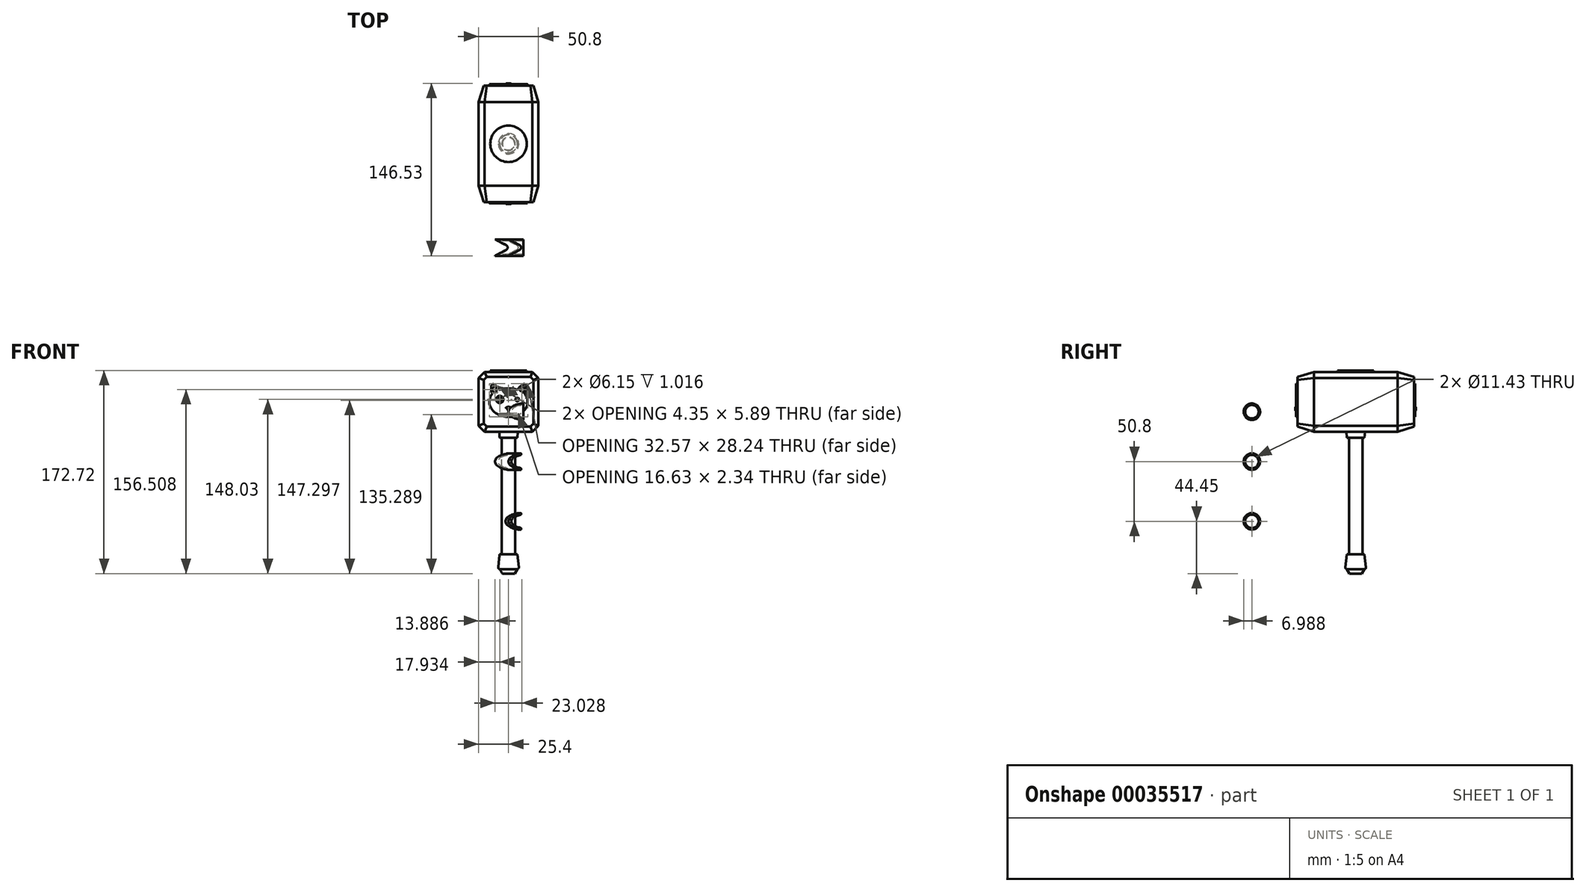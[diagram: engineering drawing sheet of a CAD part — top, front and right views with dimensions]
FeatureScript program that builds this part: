
annotation { "Feature Type Name" : "Feature", "Feature Type Description" : "" }
export const myFeature = defineFeature(function(context is Context, id is Id, definition is map)
    precondition{}
    {
        {
            var Q0;
            Q0=qCreatedBy(makeId("Front.planeOp"),FACE);
            var sketch = newSketch(context, id + "F0", { "sketchPlane" : qUnion([Q0])});
            skLineSegment(sketch, "E0.rect.bottom", {"start": v(25.4, 25.4) * mm, "end": v(-25.4, 25.4) * mm});
            skLineSegment(sketch, "E0.rect.top", {"start": v(25.4, -25.4) * mm, "end": v(-25.4, -25.4) * mm});
            skLineSegment(sketch, "E0.rect.left", {"start": v(25.4, 25.4) * mm, "end": v(25.4, -25.4) * mm});
            skLineSegment(sketch, "E0.rect.right", {"start": v(-25.4, 25.4) * mm, "end": v(-25.4, -25.4) * mm});
            skPoint(sketch, "E0.rect.middle", {"position": v(0, 0) * mm});
            skSolve(sketch);
        }
        {
            var Q0;
            Q0=makeQuery(id+"F0.imprint","IMPRINT",FACE,{"disambiguationData":[TD([[makeQuery(id+"F0.imprint","IMPRINT",EDGE,{"derivedFrom":sQuery(id+"F0.wireOp",EDGE,"E0.rect.bottom")}),1.0]])]});
            extrude(context, id + "F1", {"entities" : qUnion([Q0]), "endBound" : BoundingType.SYMMETRIC, "depth" : 71.12 * mm});
        }
        {
            var Q0;
            Q0=makeQuery(id+"F1.opExtrude","SWEPT_EDGE",EDGE,{"disambiguationData":[OSD([sQuery(id+"F0.wireOp",EDGE,"E0.rect.bottom"),sQuery(id+"F0.wireOp",EDGE,"E0.rect.left")])]});
            var Q1;
            Q1=makeQuery(id+"F1.opExtrude","SWEPT_EDGE",EDGE,{"disambiguationData":[OSD([sQuery(id+"F0.wireOp",EDGE,"E0.rect.top"),sQuery(id+"F0.wireOp",EDGE,"E0.rect.left")])]});
            var Q2;
            Q2=makeQuery(id+"F1.opExtrude","SWEPT_EDGE",EDGE,{"disambiguationData":[OSD([sQuery(id+"F0.wireOp",EDGE,"E0.rect.top"),sQuery(id+"F0.wireOp",EDGE,"E0.rect.right")])]});
            var Q3;
            Q3=makeQuery(id+"F1.opExtrude","SWEPT_EDGE",EDGE,{"disambiguationData":[OSD([sQuery(id+"F0.wireOp",EDGE,"E0.rect.bottom"),sQuery(id+"F0.wireOp",EDGE,"E0.rect.right")])]});
            chamfer(context, id + "F2", {"entities" : qUnion([Q0, Q1, Q2, Q3]), "width" : 5.08 * mm, "tangentPropagation" : true});
        }
        {
            var Q0;
            Q0=makeQuery(id+"F1.opExtrude","CAP_FACE",FACE,{"disambiguationData":[OSD([sQuery(id+"F0.wireOp",EDGE,"E0.rect.bottom"),sQuery(id+"F0.wireOp",EDGE,"E0.rect.top"),sQuery(id+"F0.wireOp",EDGE,"E0.rect.left"),sQuery(id+"F0.wireOp",EDGE,"E0.rect.right")])],"isStart":false});
            var sketch = newSketch(context, id + "F3", { "sketchPlane" : qUnion([Q0])});
            skLineSegment(sketch, "E1.0.0", {"start": v(20.32, 25.4) * mm, "end": v(-20.32, 25.4) * mm});
            skLineSegment(sketch, "E1.0.1", {"start": v(-20.32, 25.4) * mm, "end": v(-25.4, 20.32) * mm});
            skLineSegment(sketch, "E1.0.2", {"start": v(-25.4, 20.32) * mm, "end": v(-25.4, -20.32) * mm});
            skLineSegment(sketch, "E1.0.3", {"start": v(-25.4, -20.32) * mm, "end": v(-20.32, -25.4) * mm});
            skLineSegment(sketch, "E1.0.4", {"start": v(-20.32, -25.4) * mm, "end": v(20.32, -25.4) * mm});
            skLineSegment(sketch, "E1.0.5", {"start": v(20.32, -25.4) * mm, "end": v(25.4, -20.32) * mm});
            skLineSegment(sketch, "E1.0.6", {"start": v(25.4, -20.32) * mm, "end": v(25.4, 20.32) * mm});
            skLineSegment(sketch, "E1.0.7", {"start": v(25.4, 20.32) * mm, "end": v(20.32, 25.4) * mm});
            skSolve(sketch);
        }
        {
            var Q0;
            Q0=makeQuery(id+"F1.opExtrude","CAP_FACE",FACE,{"disambiguationData":[OSD([sQuery(id+"F0.wireOp",EDGE,"E0.rect.bottom"),sQuery(id+"F0.wireOp",EDGE,"E0.rect.top"),sQuery(id+"F0.wireOp",EDGE,"E0.rect.left"),sQuery(id+"F0.wireOp",EDGE,"E0.rect.right")])],"isStart":false});
            var Q1;
            Q1=makeQuery(id+"F3.imprint","IMPRINT",FACE,{"disambiguationData":[TD([[makeQuery(id+"F3.imprint","IMPRINT",EDGE,{"derivedFrom":sQuery(id+"F3.wireOp",EDGE,"E1.0.0")}),1.0]])]});
            extrude(context, id + "F4", {"entities" : qUnion([Q0, Q1]), "operationType" : NewBodyOperationType.ADD, "depth" : 13.97 * mm, "hasDraft" : true, "draftAngle" : 17 * degree, "draftPullDirection" : true});
        }
        {
            var Q0;
            Q0=makeQuery(id+"F1.opExtrude","CAP_FACE",FACE,{"disambiguationData":[OSD([sQuery(id+"F0.wireOp",EDGE,"E0.rect.bottom"),sQuery(id+"F0.wireOp",EDGE,"E0.rect.top"),sQuery(id+"F0.wireOp",EDGE,"E0.rect.left"),sQuery(id+"F0.wireOp",EDGE,"E0.rect.right")])],"isStart":true});
            var sketch = newSketch(context, id + "F5", { "sketchPlane" : qUnion([Q0])});
            skLineSegment(sketch, "E2.0.0", {"start": v(25.4, -20.32) * mm, "end": v(25.4, 20.32) * mm});
            skLineSegment(sketch, "E2.0.1", {"start": v(25.4, 20.32) * mm, "end": v(20.32, 25.4) * mm});
            skLineSegment(sketch, "E2.0.2", {"start": v(20.32, 25.4) * mm, "end": v(-20.32, 25.4) * mm});
            skLineSegment(sketch, "E2.0.3", {"start": v(-20.32, 25.4) * mm, "end": v(-25.4, 20.32) * mm});
            skLineSegment(sketch, "E2.0.4", {"start": v(-25.4, 20.32) * mm, "end": v(-25.4, -20.32) * mm});
            skLineSegment(sketch, "E2.0.5", {"start": v(-25.4, -20.32) * mm, "end": v(-20.32, -25.4) * mm});
            skLineSegment(sketch, "E2.0.6", {"start": v(-20.32, -25.4) * mm, "end": v(20.32, -25.4) * mm});
            skLineSegment(sketch, "E2.0.7", {"start": v(20.32, -25.4) * mm, "end": v(25.4, -20.32) * mm});
            skSolve(sketch);
        }
        {
            var Q0;
            Q0=makeQuery(id+"F5.imprint","IMPRINT",FACE,{"disambiguationData":[TD([[makeQuery(id+"F5.imprint","IMPRINT",EDGE,{"derivedFrom":sQuery(id+"F5.wireOp",EDGE,"E2.0.0")}),-1.0]])]});
            extrude(context, id + "F6", {"entities" : qUnion([Q0]), "operationType" : NewBodyOperationType.ADD, "depth" : 13.97 * mm, "hasDraft" : true, "draftAngle" : 17 * degree, "draftPullDirection" : true});
        }
        {
            var Q0;
            Q0=makeQuery(id+"F1.opExtrude","SWEPT_FACE",FACE,{"disambiguationData":[OSD([sQuery(id+"F0.wireOp",EDGE,"E0.rect.bottom")])]});
            var sketch = newSketch(context, id + "F7", { "sketchPlane" : qUnion([Q0])});
            skCircle(sketch, "E3", {"center": v(0, 0) * mm, "radius": 15.5 * mm});
            skSolve(sketch);
        }
        {
            var Q0;
            Q0=qSketchRegion(id+"F7",true);
            extrude(context, id + "F8", {"entities" : qUnion([Q0]), "operationType" : NewBodyOperationType.ADD, "depth" : 1.27 * mm});
        }
        {
            var Q0;
            Q0=makeQuery(id+"F1.opExtrude","SWEPT_FACE",FACE,{"disambiguationData":[OSD([sQuery(id+"F0.wireOp",EDGE,"E0.rect.top")])]});
            var sketch = newSketch(context, id + "F9", { "sketchPlane" : qUnion([Q0])});
            skCircle(sketch, "E4", {"center": v(0, 0) * mm, "radius": 7.93 * mm});
            skSolve(sketch);
        }
        {
            var Q0;
            Q0=qSketchRegion(id+"F9",true);
            extrude(context, id + "F10", {"entities" : qUnion([Q0]), "operationType" : NewBodyOperationType.ADD, "depth" : 5.08 * mm, "hasDraft" : true, "draftAngle" : 5 * degree, "draftPullDirection" : true});
        }
        {
            var Q0;
            Q0=makeQuery(id+"F10.opExtrude","CAP_FACE",FACE,{"disambiguationData":[OSD([sQuery(id+"F9.wireOp",EDGE,"E4")])],"isStart":false});
            var sketch = newSketch(context, id + "F11", { "sketchPlane" : qUnion([Q0])});
            skCircle(sketch, "E5", {"center": v(0, 0) * mm, "radius": 6.99 * mm});
            skCircle(sketch, "E6", {"center": v(0, 0) * mm, "radius": 5.72 * mm});
            skSolve(sketch);
        }
        {
            var Q0;
            Q0=makeQuery(id+"F11.imprint","IMPRINT",FACE,{"disambiguationData":[TD([[makeQuery(id+"F11.imprint","IMPRINT",EDGE,{"derivedFrom":sQuery(id+"F11.wireOp",EDGE,"E6")}),1.0]])]});
            extrude(context, id + "F12", {"entities" : qUnion([Q0]), "operationType" : NewBodyOperationType.ADD, "depth" : 99.06 * mm});
        }
        {
            var Q0;
            Q0=makeQuery(id+"F12.opExtrude","CAP_FACE",FACE,{"disambiguationData":[OSD([sQuery(id+"F11.wireOp",EDGE,"E6")])],"isStart":false});
            var sketch = newSketch(context, id + "F13", { "sketchPlane" : qUnion([Q0])});
            skCircle(sketch, "E7", {"center": v(0, 0) * mm, "radius": 7.55 * mm});
            skSolve(sketch);
        }
        {
            var Q0;
            Q0=qSketchRegion(id+"F13",true);
            extrude(context, id + "F14", {"entities" : qUnion([Q0]), "depth" : 12.7 * mm, "hasDraft" : true, "draftAngle" : 6 * degree});
        }
        {
            var Q0;
            Q0=makeQuery(id+"F14.opExtrude","CAP_EDGE",EDGE,{"disambiguationData":[OSD([sQuery(id+"F13.wireOp",EDGE,"E7")])],"isStart":false});
            fillet(context, id + "F15", {"entities" : qUnion([Q0]), "radius" : 1.27 * mm, "tangentPropagation" : true, "allowEdgeOverflow" : false});
        }
        {
            var Q0;
            Q0=makeQuery(id+"F14.opExtrude","CAP_FACE",FACE,{"disambiguationData":[OSD([sQuery(id+"F13.wireOp",EDGE,"E7")])],"isStart":false});
            var sketch = newSketch(context, id + "F16", { "sketchPlane" : qUnion([Q0])});
            skCircle(sketch, "E8.0", {"center": v(0, 0) * mm, "radius": 7.47 * mm});
            skSolve(sketch);
        }
        {
            var Q0;
            Q0=qSketchRegion(id+"F16",true);
            extrude(context, id + "F17", {"entities" : qUnion([Q0]), "operationType" : NewBodyOperationType.ADD, "depth" : 3.8 * mm, "hasDraft" : true, "draftAngle" : 30 * degree, "draftPullDirection" : true});
        }
        {
            var Q0;
            Q0=qCreatedBy(makeId("Right.planeOp"),FACE);
            var sketch = newSketch(context, id + "F18", { "sketchPlane" : qUnion([Q0])});
            skCircle(sketch, "E9", {"center": v(-88.23, -8.44) * mm, "radius": 6.99 * mm});
            skCircle(sketch, "E10", {"center": v(-88.23, -8.44) * mm, "radius": 5.72 * mm});
            skSolve(sketch);
        }
        {
            var Q0;
            Q0=qSketchRegion(id+"F18",true);
            extrude(context, id + "F19", {"entities" : qUnion([Q0]), "depth" : 12.7 * mm});
        }
        {
            var Q0;
            Q0=qCreatedBy(makeId("Top.planeOp"),FACE);
            var sketch = newSketch(context, id + "F20", { "sketchPlane" : qUnion([Q0])});
            skLineSegment(sketch, "E11.0", {"start": v(12.7, -81.25) * mm, "end": v(12.7, -95.22) * mm});
            skLineSegment(sketch, "E12.0", {"start": v(0, -81.25) * mm, "end": v(0, -88.23) * mm});
            skLineSegment(sketch, "E13", {"start": v(0, -81.25) * mm, "end": v(9.4, -86.15) * mm});
            skLineSegment(sketch, "E14.MirrorCS", {"start": v(0, -95.22) * mm, "end": v(9.4, -90.31) * mm});
            skArc(sketch, "E15", {"start": v(9.4, -90.31) * mm, "mid": v(10.65, -88.23) * mm, "end": v(9.4, -86.15) * mm});
            skPoint(sketch, "E16.orphan", {"position": v(0, -95.22) * mm});
            skLineSegment(sketch, "E17", {"start": v(0, -88.23) * mm, "end": v(0, -95.22) * mm});
            skLineSegment(sketch, "E18", {"start": v(0, -95.22) * mm, "end": v(-11.43, -95.22) * mm});
            skLineSegment(sketch, "E19", {"start": v(0, -81.25) * mm, "end": v(-11.43, -81.25) * mm});
            skLineSegment(sketch, "E20", {"start": v(-11.43, -95.22) * mm, "end": v(-2.04, -90.31) * mm});
            skLineSegment(sketch, "E21", {"start": v(0, -88.23) * mm, "end": v(8.3, -88.23) * mm});
            skLineSegment(sketch, "E22.MirrorCS", {"start": v(-11.43, -81.25) * mm, "end": v(-2.04, -86.15) * mm});
            skArc(sketch, "E23", {"start": v(-2.04, -90.31) * mm, "mid": v(-0.78, -88.23) * mm, "end": v(-2.04, -86.15) * mm});
            skSolve(sketch);
        }
        {
            var Q0;
            Q0=qSketchRegion(id+"F20",true);
            extrude(context, id + "F21", {"entities" : qUnion([Q0]), "operationType" : NewBodyOperationType.REMOVE, "oppositeDirection" : true, "depth" : 25.4 * mm});
        }
        {
            var Q0;
            Q0=qCreatedBy(makeId("Right.planeOp"),FACE);
            var sketch = newSketch(context, id + "F22", { "sketchPlane" : qUnion([Q0])});
            skCircle(sketch, "E24.0", {"center": v(-88.23, -8.44) * mm, "radius": 5.72 * mm});
            skLineSegment(sketch, "E25", {"start": v(-88.23, -8.44) * mm, "end": v(-88.23, 15.5) * mm});
            skCircle(sketch, "E26", {"center": v(-88.23, 15.5) * mm, "radius": 6.99 * mm});
            skCircle(sketch, "E27", {"center": v(-88.23, 15.5) * mm, "radius": 5.72 * mm});
            skSolve(sketch);
        }
        {
            var Q0;
            Q0=makeQuery(id+"F22.imprint","IMPRINT",FACE,{"disambiguationData":[TD([[makeQuery(id+"F22.imprint","IMPRINT",EDGE,{"derivedFrom":sQuery(id+"F22.wireOp",EDGE,"E26")}),1.0]])]});
            extrude(context, id + "F23", {"entities" : qUnion([Q0]), "endBound" : BoundingType.SYMMETRIC, "depth" : 22.86 * mm});
        }
        {
            var Q0;
            Q0=qSketchRegion(id+"F20",true);
            extrude(context, id + "F24", {"entities" : qUnion([Q0]), "operationType" : NewBodyOperationType.REMOVE, "endBound" : BoundingType.SYMMETRIC, "oppositeDirection" : true, "depth" : 508 * mm});
        }
        {
            var Q0;
            Q0=makeQuery(id+"F24.boolean.opBoolean","SPLIT",BODY,{"disambiguationData":[OD(0.0)],"derivedFrom":makeQuery(id+"F23.opExtrude","SWEPT_BODY",BODY,{"disambiguationData":[OSD([sQuery(id+"F22.wireOp",EDGE,"E26"),sQuery(id+"F22.wireOp",EDGE,"E27")])]})});
            deleteBodies(context, id + "F25", {"entities" : qUnion([Q0])});
        }
        {
            var Q0;
            Q0=qCreatedBy(makeId("Right.planeOp"),FACE);
            var sketch = newSketch(context, id + "F26", { "sketchPlane" : qUnion([Q0])});
            skCircle(sketch, "E28.0", {"center": v(-88.23, -8.44) * mm, "radius": 5.72 * mm});
            skLineSegment(sketch, "E29", {"start": v(-88.23, -8.44) * mm, "end": v(-88.23, -50.8) * mm});
            skLineSegment(sketch, "E30", {"start": v(0, 0) * mm, "end": v(-109.96, 0) * mm});
            skCircle(sketch, "E31", {"center": v(-88.23, -50.8) * mm, "radius": 6.99 * mm});
            skCircle(sketch, "E32", {"center": v(-88.23, -50.8) * mm, "radius": 5.72 * mm});
            skSolve(sketch);
        }
        {
            var Q0;
            Q0=makeQuery(id+"F26.imprint","IMPRINT",FACE,{"disambiguationData":[TD([[makeQuery(id+"F26.imprint","IMPRINT",EDGE,{"derivedFrom":sQuery(id+"F26.wireOp",EDGE,"E31")}),1.0]])]});
            extrude(context, id + "F27", {"entities" : qUnion([Q0]), "endBound" : BoundingType.SYMMETRIC, "depth" : 25.4 * mm});
        }
        {
            var Q0;
            Q0=qCreatedBy(makeId("Top.planeOp"),FACE);
            cPlane(context, id + "F28", {"entities" : qUnion([Q0]), "cplaneType" : CPlaneType.OFFSET, "offset" : 50.8 * mm, "oppositeDirection" : true, "width" : 152.4 * mm, "height" : 152.4 * mm});
        }
        {
            var Q0;
            Q0=qCreatedBy(id+"F28.planeOp",FACE);
            var sketch = newSketch(context, id + "F29", { "sketchPlane" : qUnion([Q0])});
            skLineSegment(sketch, "E33.0", {"start": v(9.4, -86.15) * mm, "end": v(0, -81.25) * mm});
            skArc(sketch, "E34.0", {"start": v(9.4, -86.15) * mm, "mid": v(10.65, -88.23) * mm, "end": v(9.4, -90.31) * mm});
            skLineSegment(sketch, "E35.0", {"start": v(9.4, -90.31) * mm, "end": v(0, -95.22) * mm});
            skLineSegment(sketch, "E36", {"start": v(12.7, -95.22) * mm, "end": v(0, -95.22) * mm});
            skLineSegment(sketch, "E37.0", {"start": v(12.7, -81.25) * mm, "end": v(12.7, -95.22) * mm});
            skLineSegment(sketch, "E38", {"start": v(0, -81.25) * mm, "end": v(12.7, -81.25) * mm});
            skLineSegment(sketch, "E39.0", {"start": v(-12.7, -81.25) * mm, "end": v(-12.7, -95.22) * mm});
            skArc(sketch, "E40.0", {"start": v(-2.04, -86.15) * mm, "mid": v(-0.78, -88.23) * mm, "end": v(-2.04, -90.31) * mm});
            skLineSegment(sketch, "E41.0", {"start": v(-2.04, -86.15) * mm, "end": v(-11.43, -81.25) * mm});
            skLineSegment(sketch, "E42.0", {"start": v(-2.04, -90.31) * mm, "end": v(-11.43, -95.22) * mm});
            skLineSegment(sketch, "E43", {"start": v(-11.43, -81.25) * mm, "end": v(-12.7, -81.25) * mm});
            skLineSegment(sketch, "E44", {"start": v(-11.43, -95.22) * mm, "end": v(-12.7, -95.22) * mm});
            skSolve(sketch);
        }
        {
            var Q0;
            Q0=qSketchRegion(id+"F29",true);
            extrude(context, id + "F30", {"entities" : qUnion([Q0]), "operationType" : NewBodyOperationType.REMOVE, "endBound" : BoundingType.SYMMETRIC, "oppositeDirection" : true, "depth" : 25.4 * mm});
        }
        {
            var Q0;
            Q0=qCreatedBy(makeId("Right.planeOp"),FACE);
            var sketch = newSketch(context, id + "F31", { "sketchPlane" : qUnion([Q0])});
            skArc(sketch, "E45.0", {"start": v(-86.15, -56.12) * mm, "mid": v(-82.52, -50.8) * mm, "end": v(-86.15, -45.48) * mm});
            skLineSegment(sketch, "E46", {"start": v(-88.23, -50.8) * mm, "end": v(-88.23, -101.6) * mm});
            skCircle(sketch, "E47", {"center": v(-88.23, -101.6) * mm, "radius": 6.99 * mm});
            skCircle(sketch, "E48", {"center": v(-88.23, -101.6) * mm, "radius": 5.72 * mm});
            skSolve(sketch);
        }
        {
            var Q0;
            Q0=makeQuery(id+"F31.imprint","IMPRINT",FACE,{"disambiguationData":[TD([[makeQuery(id+"F31.imprint","IMPRINT",EDGE,{"derivedFrom":sQuery(id+"F31.wireOp",EDGE,"E47")}),1.0]])]});
            extrude(context, id + "F32", {"entities" : qUnion([Q0]), "endBound" : BoundingType.SYMMETRIC, "depth" : 25.4 * mm});
        }
        {
            var Q0;
            Q0=qCreatedBy(id+"F28.planeOp",FACE);
            cPlane(context, id + "F33", {"entities" : qUnion([Q0]), "cplaneType" : CPlaneType.OFFSET, "offset" : 50.8 * mm, "oppositeDirection" : true, "width" : 152.4 * mm, "height" : 152.4 * mm});
        }
        {
            var Q0;
            Q0=qCreatedBy(id+"F33.planeOp",FACE);
            var sketch = newSketch(context, id + "F34", { "sketchPlane" : qUnion([Q0])});
            skLineSegment(sketch, "E49.0", {"start": v(9.4, -86.15) * mm, "end": v(0, -81.25) * mm});
            skArc(sketch, "E50.0", {"start": v(9.4, -86.15) * mm, "mid": v(10.65, -88.23) * mm, "end": v(9.4, -90.31) * mm});
            skLineSegment(sketch, "E51.0", {"start": v(9.4, -90.31) * mm, "end": v(0, -95.22) * mm});
            skLineSegment(sketch, "E52", {"start": v(-2.54, -95.22) * mm, "end": v(-2.54, -81.25) * mm});
            skLineSegment(sketch, "E53", {"start": v(-2.54, -95.22) * mm, "end": v(6.85, -90.31) * mm});
            skLineSegment(sketch, "E54.MirrorCS", {"start": v(-2.54, -81.25) * mm, "end": v(6.85, -86.15) * mm});
            skPoint(sketch, "E55.end.orphan", {"position": v(-2.54, -88.23) * mm});
            skArc(sketch, "E56", {"start": v(6.85, -90.31) * mm, "mid": v(8.11, -88.23) * mm, "end": v(6.85, -86.15) * mm});
            skLineSegment(sketch, "E57", {"start": v(-2.54, -95.22) * mm, "end": v(-16.11, -102.03) * mm});
            skLineSegment(sketch, "E58", {"start": v(-16.11, -102.03) * mm, "end": v(-15.24, -76.78) * mm});
            skLineSegment(sketch, "E59", {"start": v(-15.24, -76.78) * mm, "end": v(-2.54, -81.25) * mm});
            skLineSegment(sketch, "E60", {"start": v(0, -95.22) * mm, "end": v(15.67, -96.34) * mm});
            skLineSegment(sketch, "E61", {"start": v(15.67, -96.34) * mm, "end": v(14.05, -78.86) * mm});
            skLineSegment(sketch, "E62", {"start": v(14.05, -78.86) * mm, "end": v(0, -81.25) * mm});
            skSolve(sketch);
        }
        {
            var Q0;
            Q0=qSketchRegion(id+"F34",true);
            extrude(context, id + "F35", {"entities" : qUnion([Q0]), "operationType" : NewBodyOperationType.REMOVE, "endBound" : BoundingType.SYMMETRIC, "oppositeDirection" : true, "depth" : 25.4 * mm});
        }
        {
            var Q0;
            Q0=makeQuery(id+"F4.opExtrude","CAP_FACE",FACE,{"disambiguationData":[OSD([sQuery(id+"F0.wireOp",EDGE,"E0.rect.bottom"),sQuery(id+"F0.wireOp",EDGE,"E0.rect.top"),sQuery(id+"F0.wireOp",EDGE,"E0.rect.left"),sQuery(id+"F0.wireOp",EDGE,"E0.rect.right")])],"isStart":false});
            var sketch = newSketch(context, id + "F36", { "sketchPlane" : qUnion([Q0])});
            skEllipticalArc(sketch, "E63", {});
            skPoint(sketch, "E64", {"position": v(-13.78, 6.87) * mm});
            skLineSegment(sketch, "E65", {"start": v(0, 0) * mm, "end": v(0, 5.05) * mm});
            skPoint(sketch, "E66", {"position": v(0, -12.87) * mm});
            skPoint(sketch, "E67.MirrorP", {"position": v(13.78, 6.87) * mm});
            skLineSegment(sketch, "E68", {"start": v(0, -12.87) * mm, "end": v(0, -12.87) * mm});
            skEllipticalArc(sketch, "E69.trimOffspring", {});
            skPoint(sketch, "E70", {"position": v(-7.9, 10.08) * mm});
            skPoint(sketch, "E71.MirrorP", {"position": v(7.9, 10.08) * mm});
            skArc(sketch, "E72", {"start": v(-13.78, 15.37) * mm, "mid": v(-14.79, 11.12) * mm, "end": v(-13.78, 6.87) * mm});
            skArc(sketch, "E73", {"start": v(-7.9, 10.08) * mm, "mid": v(-10.29, 13.34) * mm, "end": v(-13.78, 15.37) * mm});
            skArc(sketch, "E74.MirrorCS", {"start": v(7.9, 10.08) * mm, "mid": v(10.29, 13.34) * mm, "end": v(13.78, 15.37) * mm});
            skArc(sketch, "E75.MirrorCS", {"start": v(13.78, 15.37) * mm, "mid": v(14.79, 11.12) * mm, "end": v(13.78, 6.87) * mm});
            skArc(sketch, "E76", {"start": v(-13.25, 13.4) * mm, "mid": v(-13.68, 10.42) * mm, "end": v(-12.89, 7.51) * mm});
            skArc(sketch, "E77", {"start": v(-9.34, 9.5) * mm, "mid": v(-11.04, 11.7) * mm, "end": v(-13.25, 13.4) * mm});
            skArc(sketch, "E78.MirrorCS", {"start": v(9.34, 9.5) * mm, "mid": v(11.04, 11.7) * mm, "end": v(13.25, 13.4) * mm});
            skArc(sketch, "E79.MirrorCS", {"start": v(13.25, 13.4) * mm, "mid": v(13.68, 10.42) * mm, "end": v(12.89, 7.51) * mm});
            skArc(sketch, "E80.trimOffspring", {"start": v(7.9, 10.08) * mm, "mid": v(0, 11.5) * mm, "end": v(-7.9, 10.08) * mm});
            skLineSegment(sketch, "E81", {"start": v(0, 2.53) * mm, "end": v(-7.47, 1.98) * mm});
            skCircle(sketch, "E82", {"center": v(-7.47, 1.98) * mm, "radius": 3.07 * mm});
            skCircle(sketch, "E83", {"center": v(-7.47, 1.98) * mm, "radius": 1.55 * mm});
            skCircle(sketch, "E84.MirrorC", {"center": v(7.47, 1.98) * mm, "radius": 1.55 * mm});
            skCircle(sketch, "E85.MirrorC", {"center": v(7.47, 1.98) * mm, "radius": 3.07 * mm});
            skArc(sketch, "E86", {"start": v(-8.55, -10.96) * mm, "mid": v(-4.2, -10.8) * mm, "end": v(0, -9.6) * mm});
            skArc(sketch, "E87", {"start": v(-8.55, -10.96) * mm, "mid": v(-4.31, -11.98) * mm, "end": v(0, -11.35) * mm});
            skArc(sketch, "E88.MirrorCS", {"start": v(8.55, -10.96) * mm, "mid": v(4.2, -10.8) * mm, "end": v(0, -9.6) * mm});
            skArc(sketch, "E89.MirrorCS", {"start": v(8.55, -10.96) * mm, "mid": v(4.31, -11.98) * mm, "end": v(0, -11.35) * mm});
            skArc(sketch, "E90", {"start": v(-9.34, 9.5) * mm, "mid": v(-11.24, 8.73) * mm, "end": v(-12.89, 7.51) * mm});
            skArc(sketch, "E91.MirrorCS", {"start": v(9.34, 9.5) * mm, "mid": v(11.24, 8.73) * mm, "end": v(12.89, 7.51) * mm});
            skArc(sketch, "E92", {"start": v(-0.22, -7.54) * mm, "mid": v(-0.39, -7.2) * mm, "end": v(-0.58, -6.89) * mm});
            skArc(sketch, "E93.MirrorCS", {"start": v(0.22, -7.54) * mm, "mid": v(0.39, -7.2) * mm, "end": v(0.58, -6.89) * mm});
            skArc(sketch, "E94", {"start": v(-0.6, -6.68) * mm, "mid": v(-0.73, -6.02) * mm, "end": v(-1.36, -5.8) * mm});
            skArc(sketch, "E95.trimOffspring", {"start": v(-1.56, -5.74) * mm, "mid": v(-1.84, -5.52) * mm, "end": v(-2.13, -5.31) * mm});
            skArc(sketch, "E96", {"start": v(2.1, -4.89) * mm, "mid": v(0, -4.32) * mm, "end": v(-2.12, -4.9) * mm});
            skArc(sketch, "E97.MirrorCS", {"start": v(0.6, -6.68) * mm, "mid": v(0.73, -6.02) * mm, "end": v(1.36, -5.8) * mm});
            skArc(sketch, "E98.trimOffspring", {"start": v(1.56, -5.74) * mm, "mid": v(1.83, -5.52) * mm, "end": v(2.12, -5.32) * mm});
            skPoint(sketch, "E99.visualSharp", {"position": v(-2.45, -5.12) * mm});
            skArc(sketch, "E99.filletArc", {"start": v(-2.12, -4.9) * mm, "mid": v(-2.24, -5.1) * mm, "end": v(-2.13, -5.31) * mm});
            skPoint(sketch, "E100.visualSharp", {"position": v(-1.47, -5.82) * mm});
            skArc(sketch, "E100.filletArc", {"start": v(-1.56, -5.74) * mm, "mid": v(-1.47, -5.8) * mm, "end": v(-1.36, -5.8) * mm});
            skPoint(sketch, "E101.visualSharp", {"position": v(-0.64, -6.78) * mm});
            skArc(sketch, "E101.filletArc", {"start": v(-0.6, -6.68) * mm, "mid": v(-0.61, -6.78) * mm, "end": v(-0.58, -6.89) * mm});
            skPoint(sketch, "E102.visualSharp", {"position": v(0, -8.1) * mm});
            skArc(sketch, "E102.filletArc", {"start": v(-0.22, -7.54) * mm, "mid": v(0, -7.68) * mm, "end": v(0.22, -7.54) * mm});
            skPoint(sketch, "E103.visualSharp", {"position": v(0.64, -6.78) * mm});
            skArc(sketch, "E103.filletArc", {"start": v(0.58, -6.89) * mm, "mid": v(0.61, -6.78) * mm, "end": v(0.6, -6.68) * mm});
            skPoint(sketch, "E104.visualSharp", {"position": v(1.47, -5.82) * mm});
            skArc(sketch, "E104.filletArc", {"start": v(1.36, -5.8) * mm, "mid": v(1.47, -5.8) * mm, "end": v(1.56, -5.74) * mm});
            skPoint(sketch, "E105.visualSharp", {"position": v(2.45, -5.12) * mm});
            skArc(sketch, "E105.filletArc", {"start": v(2.12, -5.32) * mm, "mid": v(2.23, -5.1) * mm, "end": v(2.1, -4.89) * mm});
            const initialGuessF36  = {"E63": [0, 0, -1, 0, 0.016292555257678032, 0.012874885158971939, 1.5707963267948966, 3.7046613959133827], "E69.trimOffspring": [0, 0, -1, 0, 0.016292555257678032, 0.012874885158971939, 5.720116564855996, 1.5707963267948966]};
            skSetInitialGuess(sketch, initialGuessF36);
            skSolve(sketch);
        }
        {
            var Q0;
            {var subQ4=sQuery(id+"F36.wireOp",EDGE,"E72");Q0=makeQuery(id+"F36.imprint","IMPRINT",FACE,{"disambiguationData":[TD([[makeQuery(id+"F36.imprint","IMPRINT",EDGE,{"derivedFrom":subQ4}),1.0]])]});}
            var Q1;
            Q1=makeQuery(id+"F36.imprint","IMPRINT",FACE,{"disambiguationData":[TD([[makeQuery(id+"F36.imprint","IMPRINT",EDGE,{"derivedFrom":sQuery(id+"F36.wireOp",EDGE,"E83")}),1.0]])]});
            var Q2;
            Q2=makeQuery(id+"F36.imprint","IMPRINT",FACE,{"disambiguationData":[TD([[makeQuery(id+"F36.imprint","IMPRINT",EDGE,{"derivedFrom":sQuery(id+"F36.wireOp",EDGE,"E84.MirrorC")}),-1.0]])]});
            extrude(context, id + "F37", {"entities" : qUnion([Q0, Q1, Q2]), "operationType" : NewBodyOperationType.ADD, "depth" : 1.02 * mm});
        }
        {
            var Q0;
            Q0=makeQuery(id+"F36.imprint","IMPRINT",FACE,{"disambiguationData":[TD([[makeQuery(id+"F36.imprint","IMPRINT",EDGE,{"derivedFrom":sQuery(id+"F36.wireOp",EDGE,"E92")}),-1.0]])]});
            extrude(context, id + "F38", {"entities" : qUnion([Q0]), "operationType" : NewBodyOperationType.ADD, "depth" : 1.78 * mm});
        }
        {
            var Q0;
            Q0=makeQuery(id+"F38.opExtrude","CAP_EDGE",EDGE,{"disambiguationData":[OSD([sQuery(id+"F36.wireOp",EDGE,"E105.filletArc")])],"isStart":false});
            var Q1;
            Q1=makeQuery(id+"F38.opExtrude","CAP_EDGE",EDGE,{"disambiguationData":[OSD([sQuery(id+"F36.wireOp",EDGE,"E96")])],"isStart":false});
            var Q2;
            Q2=makeQuery(id+"F38.opExtrude","CAP_EDGE",EDGE,{"disambiguationData":[OSD([sQuery(id+"F36.wireOp",EDGE,"E99.filletArc")])],"isStart":false});
            var Q3;
            Q3=makeQuery(id+"F38.opExtrude","CAP_EDGE",EDGE,{"disambiguationData":[OSD([sQuery(id+"F36.wireOp",EDGE,"E95.trimOffspring")])],"isStart":false});
            var Q4;
            Q4=makeQuery(id+"F38.opExtrude","CAP_EDGE",EDGE,{"disambiguationData":[OSD([sQuery(id+"F36.wireOp",EDGE,"E97.MirrorCS")])],"isStart":false});
            var Q5;
            Q5=makeQuery(id+"F38.opExtrude","CAP_EDGE",EDGE,{"disambiguationData":[OSD([sQuery(id+"F36.wireOp",EDGE,"E98.trimOffspring")])],"isStart":false});
            var Q6;
            Q6=makeQuery(id+"F38.opExtrude","CAP_EDGE",EDGE,{"disambiguationData":[OSD([sQuery(id+"F36.wireOp",EDGE,"E104.filletArc")])],"isStart":false});
            var Q7;
            Q7=makeQuery(id+"F38.opExtrude","CAP_FACE",FACE,{"disambiguationData":[OSD([sQuery(id+"F36.wireOp",EDGE,"E92"),sQuery(id+"F36.wireOp",EDGE,"E93.MirrorCS"),sQuery(id+"F36.wireOp",EDGE,"E94"),sQuery(id+"F36.wireOp",EDGE,"E95.trimOffspring"),sQuery(id+"F36.wireOp",EDGE,"E96"),sQuery(id+"F36.wireOp",EDGE,"E97.MirrorCS"),sQuery(id+"F36.wireOp",EDGE,"E98.trimOffspring"),sQuery(id+"F36.wireOp",EDGE,"E99.filletArc"),sQuery(id+"F36.wireOp",EDGE,"E100.filletArc"),sQuery(id+"F36.wireOp",EDGE,"E101.filletArc"),sQuery(id+"F36.wireOp",EDGE,"E102.filletArc"),sQuery(id+"F36.wireOp",EDGE,"E103.filletArc"),sQuery(id+"F36.wireOp",EDGE,"E104.filletArc"),sQuery(id+"F36.wireOp",EDGE,"E105.filletArc")])],"isStart":false});
            fillet(context, id + "F39", {"entities" : qUnion([Q0, Q1, Q2, Q3, Q4, Q5, Q6, Q7]), "radius" : 0.5 * mm, "tangentPropagation" : true, "allowEdgeOverflow" : false});
        }
        {
            var Q0;
            {var subQ0=sQuery(id+"F0.wireOp",EDGE,"E0.rect.bottom");var subQ1=sQuery(id+"F0.wireOp",EDGE,"E0.rect.top");var subQ2=sQuery(id+"F0.wireOp",EDGE,"E0.rect.left");var subQ3=sQuery(id+"F0.wireOp",EDGE,"E0.rect.right");Q0=makeQuery(id+"F37.boolean.opBoolean","SPLIT",FACE,{"disambiguationData":[TD([makeQuery(id+"F4.opExtrude","SWEPT_FACE",FACE,{"disambiguationData":[OSD([subQ0])]})])],"derivedFrom":makeQuery(id+"F4.opExtrude","CAP_FACE",FACE,{"disambiguationData":[OSD([subQ0,subQ1,subQ2,subQ3])],"isStart":false})});}
            var sketch = newSketch(context, id + "F40", { "sketchPlane" : qUnion([Q0])});
            skEllipticalArc(sketch, "E106.0", {});
            skEllipticalArc(sketch, "E107.0", {});
            skArc(sketch, "E108", {"start": v(-8.31, -10.98) * mm, "mid": v(-4.2, -11.93) * mm, "end": v(0, -11.35) * mm});
            skLineSegment(sketch, "E109", {"start": v(0, -11.35) * mm, "end": v(0, -12.87) * mm});
            skPoint(sketch, "E110.0.start.orphan", {"position": v(-8.55, -10.96) * mm});
            skPoint(sketch, "E111.0.end.orphan", {"position": v(0, -11.35) * mm});
            skPoint(sketch, "E111.0.start.orphan", {"position": v(8.55, -10.96) * mm});
            skArc(sketch, "E112.MirrorCS", {"start": v(8.31, -10.98) * mm, "mid": v(4.2, -11.93) * mm, "end": v(0, -11.35) * mm});
            skLineSegment(sketch, "E113", {"start": v(-8.31, -10.98) * mm, "end": v(-8.55, -10.96) * mm});
            skLineSegment(sketch, "E114", {"start": v(8.31, -10.98) * mm, "end": v(8.55, -10.96) * mm});
            const initialGuessF40  = {"E106.0": [0, 0, -1, 0, 0.016292555257678032, 0.012874885158971939, 5.720116564855996, 1.5707963267948966], "E107.0": [0, 0, -1, 0, 0.016292555257678032, 0.012874885158971939, 1.5707963267948966, 3.7046613959133823]};
            skSetInitialGuess(sketch, initialGuessF40);
            skSolve(sketch);
        }
        {
            var Q0;
            Q0 = qSketchRegion(id + "F40", true);
            extrude(context, id + "F41", {"entities" : qUnion([Q0]), "operationType" : NewBodyOperationType.ADD, "depth" : 1.02 * mm});
        }
        {
            var Q0;
            Q0=qCreatedBy(makeId("Right.planeOp"),FACE);
            var sketch = newSketch(context, id + "F42", { "sketchPlane" : qUnion([Q0])});
            skLineSegment(sketch, "E115", {"start": v(0, 0) * mm, "end": v(0, -126) * mm});
            skLineSegment(sketch, "E116.0", {"start": v(7.55, -129.54) * mm, "end": v(-7.55, -129.54) * mm});
            skLineSegment(sketch, "E117", {"start": v(0, -126) * mm, "end": v(0, -129.54) * mm});
            skLineSegment(sketch, "E118", {"start": v(0, -129.54) * mm, "end": v(78.8, -129.54) * mm});
            skLineSegment(sketch, "E119", {"start": v(78.8, -129.54) * mm, "end": v(78.8, 49.1) * mm});
            skLineSegment(sketch, "E120", {"start": v(78.8, 49.1) * mm, "end": v(0, 49.1) * mm});
            skLineSegment(sketch, "E121", {"start": v(0, 49.1) * mm, "end": v(0, 0) * mm});
            skSolve(sketch);
        }
        {
            var Q0;
            Q0 = qSketchRegion(id + "F42", true);
            extrude(context, id + "F43", {"entities" : qUnion([Q0]), "operationType" : NewBodyOperationType.REMOVE, "endBound" : BoundingType.SYMMETRIC, "oppositeDirection" : true, "depth" : 101.6 * mm});
        }
        {
            var Q0;
            Q0=makeQuery(id+"F1.opExtrude","SWEPT_BODY",BODY,{"disambiguationData":[OSD([sQuery(id+"F0.wireOp",EDGE,"E0.rect.bottom"),sQuery(id+"F0.wireOp",EDGE,"E0.rect.top"),sQuery(id+"F0.wireOp",EDGE,"E0.rect.left"),sQuery(id+"F0.wireOp",EDGE,"E0.rect.right")])]});
            var Q1;
            Q1=makeQuery(id+"F43.boolean.opBoolean","COPY",FACE,{"derivedFrom":makeQuery(id+"F43.opExtrude","SWEPT_FACE",FACE,{"disambiguationData":[OSD([sQuery(id+"F42.wireOp",EDGE,"E115"),sQuery(id+"F42.wireOp",EDGE,"E117"),sQuery(id+"F42.wireOp",EDGE,"E121")])]})});
            mirror(context, id + "F44", {"operationType" : NewBodyOperationType.ADD, "entities" : qUnion([Q0]), "mirrorPlane" : qUnion([Q1])});
        }
    });
